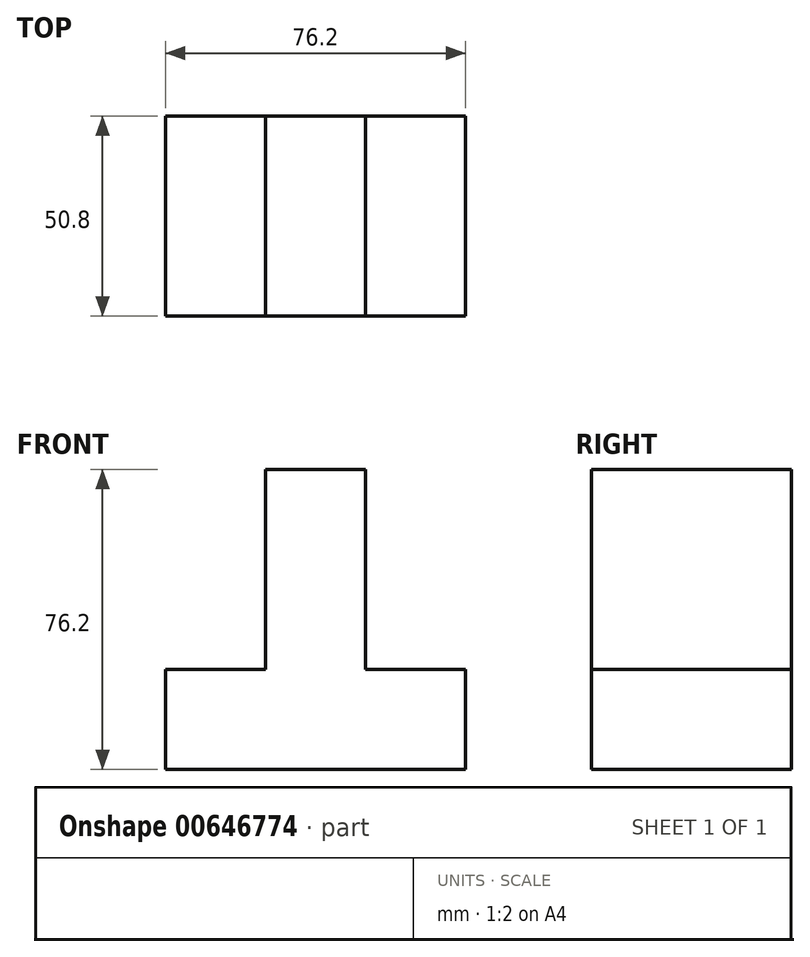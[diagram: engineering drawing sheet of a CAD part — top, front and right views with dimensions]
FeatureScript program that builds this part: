
annotation { "Feature Type Name" : "Feature", "Feature Type Description" : "" }
export const myFeature = defineFeature(function(context is Context, id is Id, definition is map)
    precondition{}
    {
        {
            var Q0;
            Q0=qCreatedBy(makeId("Front.planeOp"),FACE);
            var sketch = newSketch(context, id + "F0", { "sketchPlane" : qUnion([Q0])});
            skLineSegment(sketch, "E0", {"start": v(12.13, 60.83) * mm, "end": v(12.13, 10.03) * mm});
            skLineSegment(sketch, "E1", {"start": v(12.13, 10.03) * mm, "end": v(37.53, 10.03) * mm});
            skLineSegment(sketch, "E2", {"start": v(37.53, 10.03) * mm, "end": v(37.53, -15.37) * mm});
            skLineSegment(sketch, "E3", {"start": v(37.53, -15.37) * mm, "end": v(-38.67, -15.37) * mm});
            skLineSegment(sketch, "E4", {"start": v(-38.67, -15.37) * mm, "end": v(-38.67, 10.03) * mm});
            skLineSegment(sketch, "E5", {"start": v(-38.67, 10.03) * mm, "end": v(-13.27, 10.03) * mm});
            skLineSegment(sketch, "E6", {"start": v(-13.27, 10.03) * mm, "end": v(-13.27, 60.83) * mm});
            skLineSegment(sketch, "E7", {"start": v(-13.27, 60.83) * mm, "end": v(12.13, 60.83) * mm});
            skSolve(sketch);
        }
        {
            var Q0;
            Q0=makeQuery(id+"F0.imprint","IMPRINT",FACE,{"disambiguationData":[TD([[makeQuery(id+"F0.imprint","IMPRINT",EDGE,{"derivedFrom":sQuery(id+"F0.wireOp",EDGE,"E0")}),-1.0]])]});
            extrude(context, id + "F1", {"entities" : qUnion([Q0]), "depth" : 50.8 * mm, "offsetDistance" : 25.4 * mm});
        }
    });
